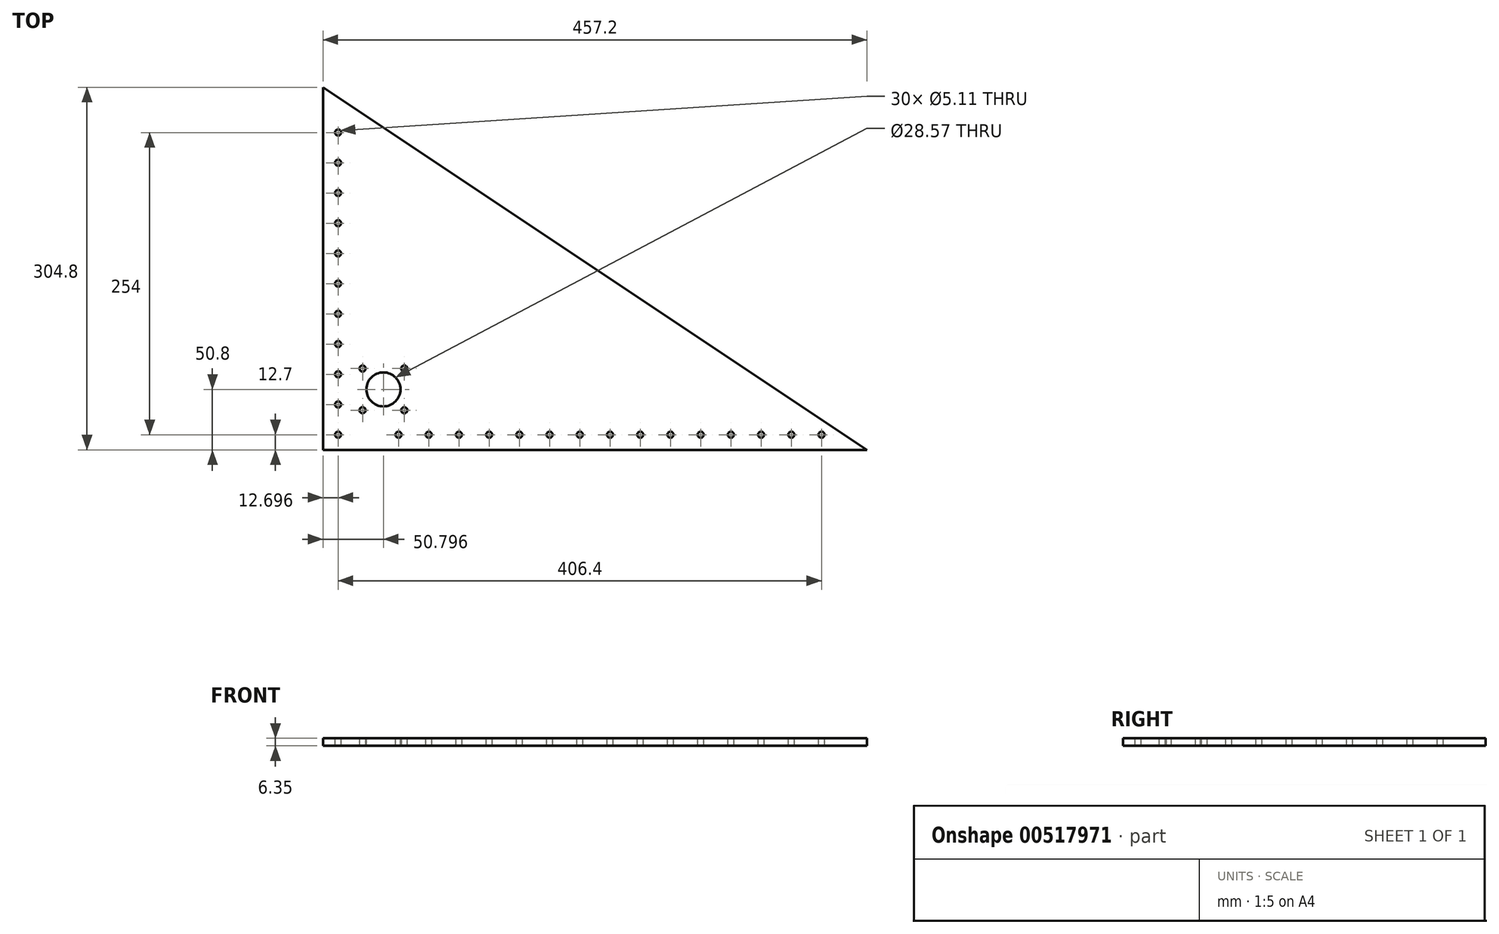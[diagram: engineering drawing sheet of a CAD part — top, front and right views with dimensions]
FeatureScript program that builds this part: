
annotation { "Feature Type Name" : "Feature", "Feature Type Description" : "" }
export const myFeature = defineFeature(function(context is Context, id is Id, definition is map)
    precondition{}
    {
        {
            var Q0;
            Q0=qCreatedBy(makeId("Top.planeOp"),FACE);
            var sketch = newSketch(context, id + "F0", { "sketchPlane" : qUnion([Q0])});
            skLineSegment(sketch, "E0", {"start": v(-234.6, 117.46) * mm, "end": v(-234.6, -187.34) * mm});
            skLineSegment(sketch, "E1", {"start": v(-234.6, -187.34) * mm, "end": v(222.6, -187.34) * mm});
            skLineSegment(sketch, "E2", {"start": v(222.6, -187.34) * mm, "end": v(-234.6, 117.46) * mm});
            skSolve(sketch);
        }
        {
            var Q0;
            Q0 = qSketchRegion(id + "F0", true);
            extrude(context, id + "F1", {"entities" : qUnion([Q0]), "depth" : 6.35 * mm, "offsetDistance" : 25.4 * mm});
        }
        {
            var Q0;
            Q0=makeQuery(id+"F1.opExtrude","CAP_FACE",FACE,{"disambiguationData":[OSD([sQuery(id+"F0.wireOp",EDGE,"E0"),sQuery(id+"F0.wireOp",EDGE,"E1"),sQuery(id+"F0.wireOp",EDGE,"E2")])],"isStart":false});
            var sketch = newSketch(context, id + "F2", { "sketchPlane" : qUnion([Q0])});
            skCircle(sketch, "E3", {"center": v(-221.9, -174.64) * mm, "radius": 2.55 * mm});
            skCircle(sketch, "E4.0.1.0", {"center": v(-221.9, -149.24) * mm, "radius": 2.55 * mm});
            skCircle(sketch, "E4.0.2.0", {"center": v(-221.9, -123.84) * mm, "radius": 2.55 * mm});
            skCircle(sketch, "E4.0.3.0", {"center": v(-221.9, -98.44) * mm, "radius": 2.55 * mm});
            skCircle(sketch, "E4.0.4.0", {"center": v(-221.9, -73.04) * mm, "radius": 2.55 * mm});
            skCircle(sketch, "E4.0.5.0", {"center": v(-221.9, -47.64) * mm, "radius": 2.55 * mm});
            skCircle(sketch, "E4.0.6.0", {"center": v(-221.9, -22.24) * mm, "radius": 2.55 * mm});
            skCircle(sketch, "E4.0.7.0", {"center": v(-221.9, 3.16) * mm, "radius": 2.55 * mm});
            skCircle(sketch, "E4.0.8.0", {"center": v(-221.9, 28.56) * mm, "radius": 2.55 * mm});
            skCircle(sketch, "E4.0.9.0", {"center": v(-221.9, 53.96) * mm, "radius": 2.55 * mm});
            skCircle(sketch, "E4.0.10.0", {"center": v(-221.9, 79.36) * mm, "radius": 2.55 * mm});
            skLineSegment(sketch, "E4.direction1", {"start": v(-221.9, -174.64) * mm, "end": v(-196.5, -174.64) * mm, "construction": true});
            skLineSegment(sketch, "E4.direction2", {"start": v(-221.9, -174.64) * mm, "end": v(-221.9, -149.24) * mm, "construction": true});
            skCircle(sketch, "E5.1.0.0", {"center": v(-196.5, -174.64) * mm, "radius": 2.55 * mm});
            skCircle(sketch, "E5.2.0.0", {"center": v(-171.1, -174.64) * mm, "radius": 2.55 * mm});
            skCircle(sketch, "E5.3.0.0", {"center": v(-145.7, -174.64) * mm, "radius": 2.55 * mm});
            skCircle(sketch, "E5.4.0.0", {"center": v(-120.3, -174.64) * mm, "radius": 2.55 * mm});
            skCircle(sketch, "E5.5.0.0", {"center": v(-94.9, -174.64) * mm, "radius": 2.55 * mm});
            skCircle(sketch, "E5.6.0.0", {"center": v(-69.5, -174.64) * mm, "radius": 2.55 * mm});
            skCircle(sketch, "E5.7.0.0", {"center": v(-44.1, -174.64) * mm, "radius": 2.55 * mm});
            skCircle(sketch, "E5.8.0.0", {"center": v(-18.7, -174.64) * mm, "radius": 2.55 * mm});
            skCircle(sketch, "E5.9.0.0", {"center": v(6.7, -174.64) * mm, "radius": 2.55 * mm});
            skCircle(sketch, "E5.10.0.0", {"center": v(32.1, -174.64) * mm, "radius": 2.55 * mm});
            skCircle(sketch, "E5.11.0.0", {"center": v(57.5, -174.64) * mm, "radius": 2.55 * mm});
            skCircle(sketch, "E5.12.0.0", {"center": v(82.9, -174.64) * mm, "radius": 2.55 * mm});
            skCircle(sketch, "E5.13.0.0", {"center": v(108.3, -174.64) * mm, "radius": 2.55 * mm});
            skCircle(sketch, "E5.14.0.0", {"center": v(133.7, -174.64) * mm, "radius": 2.55 * mm});
            skCircle(sketch, "E5.15.0.0", {"center": v(159.1, -174.64) * mm, "radius": 2.55 * mm});
            skCircle(sketch, "E5.16.0.0", {"center": v(184.5, -174.64) * mm, "radius": 2.55 * mm});
            skSolve(sketch);
        }
        {
            var Q0;
            Q0=sQuery(id+"F2.wireOp",VERTEX,"E4.0.9.0.center");
            var Q1;
            Q1=sQuery(id+"F2.wireOp",VERTEX,"E5.6.0.0.center");
            var Q2;
            Q2=sQuery(id+"F2.wireOp",VERTEX,"E5.12.0.0.center");
            var Q3;
            Q3=sQuery(id+"F2.wireOp",VERTEX,"E4.0.6.0.center");
            var Q4;
            Q4=sQuery(id+"F2.wireOp",VERTEX,"E4.0.5.0.center");
            var Q5;
            Q5=sQuery(id+"F2.wireOp",VERTEX,"E4.0.4.0.center");
            var Q6;
            Q6=sQuery(id+"F2.wireOp",VERTEX,"E4.0.8.0.center");
            var Q7;
            Q7=sQuery(id+"F2.wireOp",VERTEX,"E5.2.0.0.center");
            var Q8;
            Q8=sQuery(id+"F2.wireOp",VERTEX,"E4.0.7.0.center");
            var Q9;
            Q9=sQuery(id+"F2.wireOp",VERTEX,"E5.13.0.0.center");
            var Q10;
            Q10=sQuery(id+"F2.wireOp",VERTEX,"E5.4.0.0.center");
            var Q11;
            Q11=sQuery(id+"F2.wireOp",VERTEX,"E5.15.0.0.center");
            var Q12;
            Q12=sQuery(id+"F2.wireOp",VERTEX,"E5.8.0.0.center");
            var Q13;
            Q13=sQuery(id+"F2.wireOp",VERTEX,"E5.5.0.0.center");
            var Q14;
            Q14=sQuery(id+"F2.wireOp",VERTEX,"E5.10.0.0.center");
            var Q15;
            Q15=sQuery(id+"F2.wireOp",VERTEX,"E4.0.2.0.center");
            var Q16;
            Q16=sQuery(id+"F2.wireOp",VERTEX,"E3.center");
            var Q17;
            Q17=sQuery(id+"F2.wireOp",VERTEX,"E4.0.3.0.center");
            var Q18;
            Q18=sQuery(id+"F2.wireOp",VERTEX,"E5.16.0.0.center");
            var Q19;
            Q19=sQuery(id+"F2.wireOp",VERTEX,"E4.direction1.end");
            var Q20;
            Q20=sQuery(id+"F2.wireOp",VERTEX,"E5.14.0.0.center");
            var Q21;
            Q21=sQuery(id+"F2.wireOp",VERTEX,"E5.11.0.0.center");
            var Q22;
            Q22=sQuery(id+"F2.wireOp",VERTEX,"E5.3.0.0.center");
            var Q23;
            Q23=sQuery(id+"F2.wireOp",VERTEX,"E5.7.0.0.center");
            var Q24;
            Q24=sQuery(id+"F2.wireOp",VERTEX,"E5.9.0.0.center");
            var Q25;
            Q25=sQuery(id+"F2.wireOp",VERTEX,"E4.direction2.end");
            var Q26;
            Q26=sQuery(id+"F2.wireOp",VERTEX,"E4.0.10.0.center");
            var Q27;
            Q27=makeQuery(id+"F1.opExtrude","SWEPT_BODY",BODY,{"disambiguationData":[OSD([sQuery(id+"F0.wireOp",EDGE,"E0"),sQuery(id+"F0.wireOp",EDGE,"E1"),sQuery(id+"F0.wireOp",EDGE,"E2")])]});
            hole(context, id + "F3", {"style" : HoleStyle.SIMPLE, "endStyle" : HoleEndStyle.THROUGH, "holeDiameter" : 5.1 * mm, "isTappedThrough" : true, "tappedDepth" : 12.7 * mm, "tapClearance" : 3, "locations" : qUnion([Q0, Q1, Q2, Q3, Q4, Q5, Q6, Q7, Q8, Q9, Q10, Q11, Q12, Q13, Q14, Q15, Q16, Q17, Q18, Q19, Q20, Q21, Q22, Q23, Q24, Q25, Q26]), "scope" : qUnion([Q27])});
        }
        {
            var Q0;
            Q0=makeQuery(id+"F1.opExtrude","CAP_FACE",FACE,{"disambiguationData":[OSD([sQuery(id+"F0.wireOp",EDGE,"E0"),sQuery(id+"F0.wireOp",EDGE,"E1"),sQuery(id+"F0.wireOp",EDGE,"E2")])],"isStart":false});
            var sketch = newSketch(context, id + "F4", { "sketchPlane" : qUnion([Q0])});
            skCircle(sketch, "E6", {"center": v(-183.8, -136.54) * mm, "radius": 14.29 * mm});
            skLineSegment(sketch, "E7.bottom", {"start": v(-166.27, -154.07) * mm, "end": v(-201.32, -154.07) * mm});
            skLineSegment(sketch, "E7.top", {"start": v(-166.27, -119.01) * mm, "end": v(-201.32, -119.01) * mm});
            skLineSegment(sketch, "E7.left", {"start": v(-166.27, -154.07) * mm, "end": v(-166.27, -119.01) * mm});
            skLineSegment(sketch, "E7.right", {"start": v(-201.32, -154.07) * mm, "end": v(-201.32, -119.01) * mm});
            skCircle(sketch, "E8", {"center": v(-201.32, -119.01) * mm, "radius": 2.55 * mm});
            skCircle(sketch, "E9", {"center": v(-166.27, -119.01) * mm, "radius": 2.55 * mm});
            skCircle(sketch, "E10", {"center": v(-201.32, -154.07) * mm, "radius": 2.55 * mm});
            skCircle(sketch, "E11", {"center": v(-166.27, -154.07) * mm, "radius": 2.55 * mm});
            skSolve(sketch);
        }
        {
            var Q0;
            Q0=sQuery(id+"F4.wireOp",VERTEX,"E8.center");
            var Q1;
            Q1=sQuery(id+"F4.wireOp",VERTEX,"E9.center");
            var Q2;
            Q2=sQuery(id+"F4.wireOp",VERTEX,"E10.center");
            var Q3;
            Q3=sQuery(id+"F4.wireOp",VERTEX,"E11.center");
            var Q4;
            Q4=makeQuery(id+"F1.opExtrude","SWEPT_BODY",BODY,{"disambiguationData":[OSD([sQuery(id+"F0.wireOp",EDGE,"E0"),sQuery(id+"F0.wireOp",EDGE,"E1"),sQuery(id+"F0.wireOp",EDGE,"E2")])]});
            hole(context, id + "F5", {"style" : HoleStyle.SIMPLE, "endStyle" : HoleEndStyle.THROUGH, "holeDiameter" : 5.1 * mm, "isTappedThrough" : true, "tappedDepth" : 12.7 * mm, "tapClearance" : 3, "locations" : qUnion([Q0, Q1, Q2, Q3]), "scope" : qUnion([Q4])});
        }
        {
            var Q0;
            Q0=sQuery(id+"F4.wireOp",VERTEX,"E6.center");
            var Q1;
            Q1=makeQuery(id+"F1.opExtrude","SWEPT_BODY",BODY,{"disambiguationData":[OSD([sQuery(id+"F0.wireOp",EDGE,"E0"),sQuery(id+"F0.wireOp",EDGE,"E1"),sQuery(id+"F0.wireOp",EDGE,"E2")])]});
            hole(context, id + "F6", {"style" : HoleStyle.SIMPLE, "endStyle" : HoleEndStyle.THROUGH, "holeDiameter" : 28.57 * mm, "isTappedThrough" : true, "tappedDepth" : 12.7 * mm, "tapClearance" : 3, "locations" : qUnion([Q0]), "scope" : qUnion([Q1])});
        }
    });
